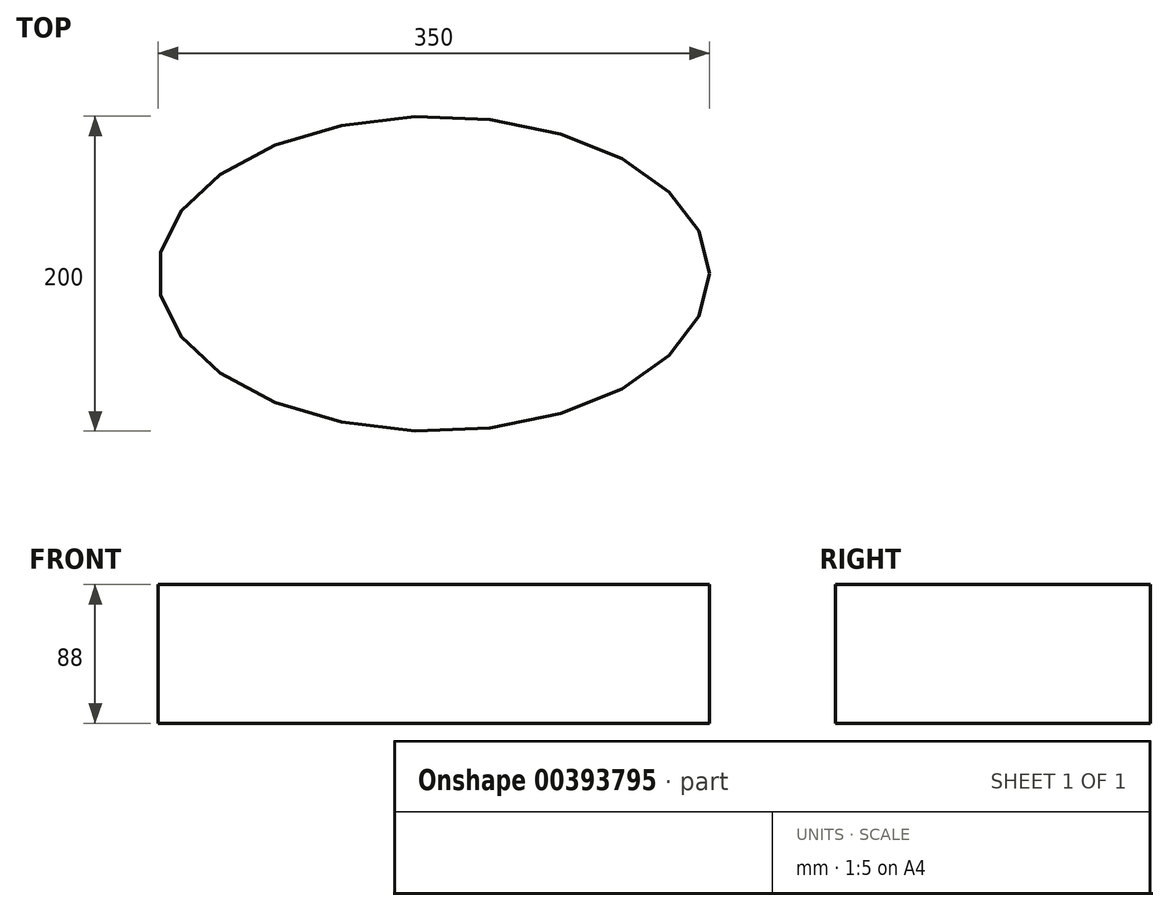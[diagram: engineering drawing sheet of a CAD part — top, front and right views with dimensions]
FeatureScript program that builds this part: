
annotation { "Feature Type Name" : "Feature", "Feature Type Description" : "" }
export const myFeature = defineFeature(function(context is Context, id is Id, definition is map)
    precondition{}
    {
        {
            var Q0;
            Q0=qCreatedBy(makeId("Top.planeOp"), FACE);
            var sketch = newSketch(context, id + "F0", { "sketchPlane" : qUnion([Q0])});
            skEllipse(sketch, "E0", {"center": v(0, 0) * mm, "majorRadius": 175 * mm, "minorRadius": 100 * mm, "majorAxis": v(1, 0)});
            skLineSegment(sketch, "E1", {"start": v(-175, 0) * mm, "end": v(175, 0) * mm, "construction": true});
            skSolve(sketch);
        }
        {
            var Q0;
            Q0 = qSketchRegion(id + "F0", true);
            extrude(context, id + "F1", {"entities" : qUnion([Q0]), "oppositeDirection" : true, "depth" : 88 * mm, "offsetDistance" : 25 * mm});
        }
    });
